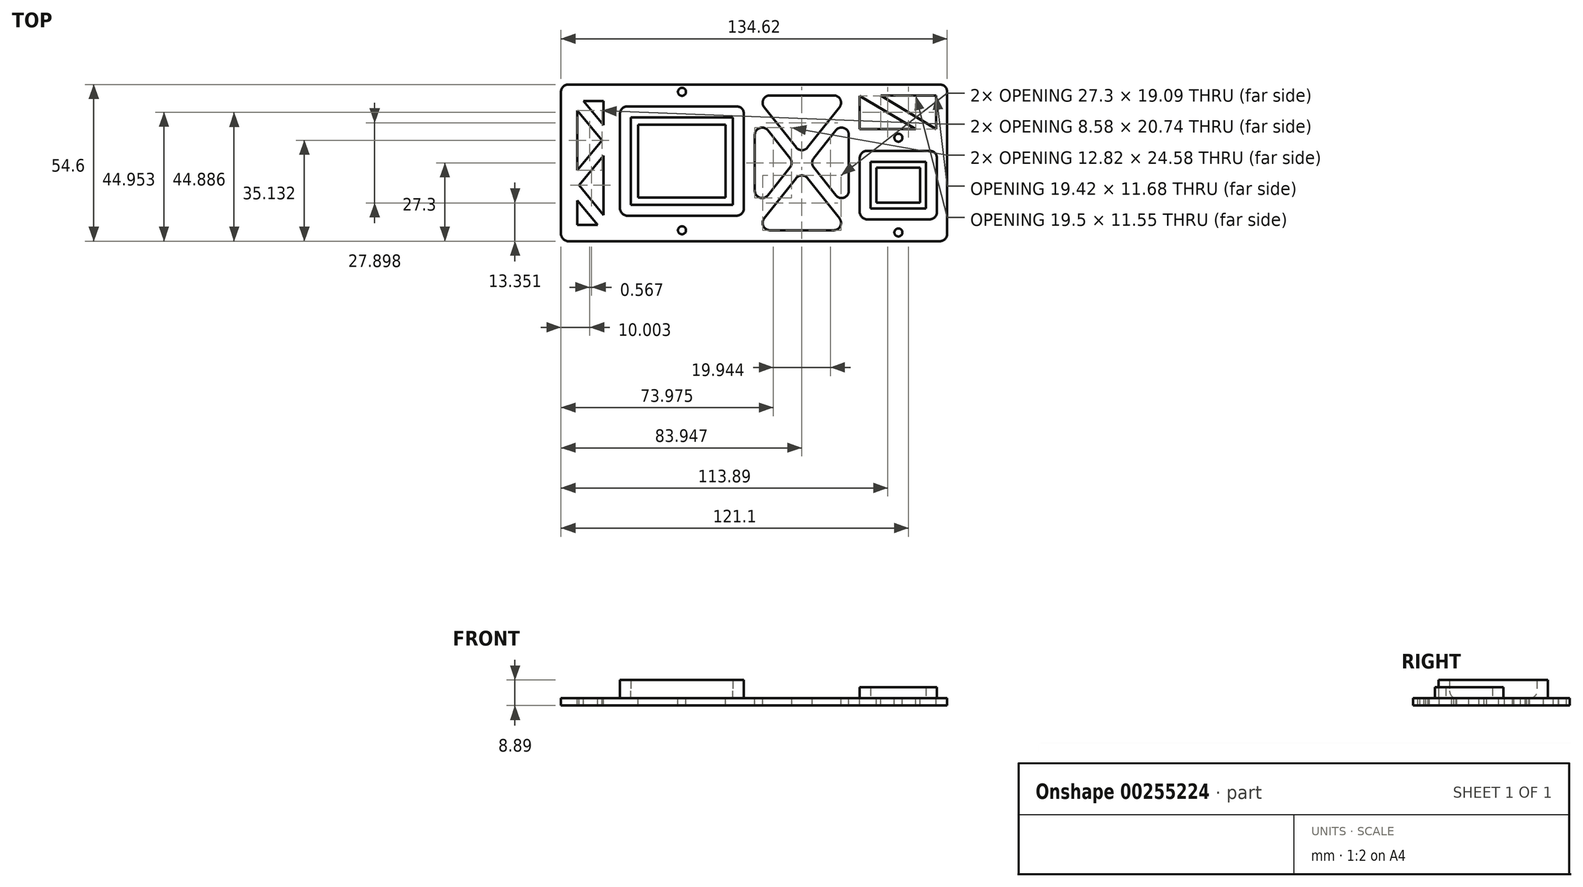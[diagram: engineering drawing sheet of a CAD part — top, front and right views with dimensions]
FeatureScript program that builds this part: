
annotation { "Feature Type Name" : "Feature", "Feature Type Description" : "" }
export const myFeature = defineFeature(function(context is Context, id is Id, definition is map)
    precondition{}
    {
        {
            var Q0;
            Q0=qCreatedBy(makeId("Top.planeOp"),FACE);
            var sketch = newSketch(context, id + "F0", { "sketchPlane" : qUnion([Q0])});
            skLineSegment(sketch, "E0.bottom", {"start": v(67.31, 27.3) * mm, "end": v(-67.31, 27.3) * mm});
            skLineSegment(sketch, "E0.top", {"start": v(67.31, -27.3) * mm, "end": v(-67.31, -27.3) * mm});
            skLineSegment(sketch, "E0.left", {"start": v(67.31, 27.3) * mm, "end": v(67.31, -27.3) * mm});
            skLineSegment(sketch, "E0.right", {"start": v(-67.31, 27.3) * mm, "end": v(-67.31, -27.3) * mm});
            skPoint(sketch, "E0.middle", {"position": v(0, 0) * mm});
            skSolve(sketch);
        }
        {
            var Q0;
            Q0=makeQuery(id+"F0.imprint","IMPRINT",FACE,{"disambiguationData":[TD([[makeQuery(id+"F0.imprint","IMPRINT",EDGE,{"derivedFrom":sQuery(id+"F0.wireOp",EDGE,"E0.bottom")}),1.0]])]});
            extrude(context, id + "F1", {"entities" : qUnion([Q0]), "oppositeDirection" : true, "depth" : 2.54 * mm});
        }
        {
            var Q0;
            Q0=makeQuery(id+"F1.opExtrude","CAP_FACE",FACE,{"disambiguationData":[OSD([sQuery(id+"F0.wireOp",EDGE,"E0.bottom"),sQuery(id+"F0.wireOp",EDGE,"E0.top"),sQuery(id+"F0.wireOp",EDGE,"E0.left"),sQuery(id+"F0.wireOp",EDGE,"E0.right")])],"isStart":true});
            var sketch = newSketch(context, id + "F2", { "sketchPlane" : qUnion([Q0])});
            skLineSegment(sketch, "E1.bottom", {"start": v(-7.37, -14.6) * mm, "end": v(-42.93, -14.6) * mm});
            skLineSegment(sketch, "E1.top", {"start": v(-7.37, 15.88) * mm, "end": v(-42.93, 15.88) * mm});
            skLineSegment(sketch, "E1.left", {"start": v(-7.37, -14.6) * mm, "end": v(-7.37, 15.88) * mm});
            skLineSegment(sketch, "E1.right", {"start": v(-42.93, -14.6) * mm, "end": v(-42.93, 15.88) * mm});
            skPoint(sketch, "E1.middle", {"position": v(-25.15, 0.64) * mm});
            skPoint(sketch, "E2.0", {"position": v(-67.31, -27.3) * mm});
            skLineSegment(sketch, "E3.bottom", {"start": v(59.94, -15.87) * mm, "end": v(40.64, -15.87) * mm});
            skLineSegment(sketch, "E3.top", {"start": v(59.94, 0.38) * mm, "end": v(40.64, 0.38) * mm});
            skLineSegment(sketch, "E3.left", {"start": v(59.94, -15.87) * mm, "end": v(59.94, 0.38) * mm});
            skLineSegment(sketch, "E3.right", {"start": v(40.64, -15.87) * mm, "end": v(40.64, 0.38) * mm});
            skPoint(sketch, "E3.middle", {"position": v(50.3, -7.75) * mm});
            skLineSegment(sketch, "E4.0", {"start": v(-46.74, -18.41) * mm, "end": v(-46.74, 19.69) * mm});
            skLineSegment(sketch, "E4.1", {"start": v(-3.56, -18.41) * mm, "end": v(-46.74, -18.41) * mm});
            skLineSegment(sketch, "E4.2", {"start": v(-3.56, -18.41) * mm, "end": v(-3.56, 19.69) * mm});
            skLineSegment(sketch, "E4.3", {"start": v(-3.56, 19.69) * mm, "end": v(-46.74, 19.69) * mm});
            skLineSegment(sketch, "E5.0", {"start": v(63.75, -19.68) * mm, "end": v(63.75, 4.2) * mm});
            skLineSegment(sketch, "E5.1", {"start": v(63.75, -19.68) * mm, "end": v(36.83, -19.68) * mm});
            skLineSegment(sketch, "E5.2", {"start": v(36.83, -19.68) * mm, "end": v(36.83, 4.2) * mm});
            skLineSegment(sketch, "E5.3", {"start": v(63.75, 4.2) * mm, "end": v(36.83, 4.2) * mm});
            skCircle(sketch, "E6", {"center": v(-25.15, 24.77) * mm, "radius": 1.4 * mm});
            skCircle(sketch, "E7", {"center": v(-25.15, -23.5) * mm, "radius": 1.4 * mm});
            skCircle(sketch, "E8", {"center": v(50.3, 8.76) * mm, "radius": 1.4 * mm});
            skCircle(sketch, "E9", {"center": v(50.3, -24.26) * mm, "radius": 1.4 * mm});
            skPoint(sketch, "E10", {"position": v(-25.15, 19.69) * mm});
            skPoint(sketch, "E11", {"position": v(50.3, -19.68) * mm});
            skLineSegment(sketch, "E12", {"start": v(50.3, 8.76) * mm, "end": v(50.3, -7.75) * mm, "construction": true});
            skLineSegment(sketch, "E13", {"start": v(50.3, -24.26) * mm, "end": v(50.3, -7.75) * mm, "construction": true});
            skLineSegment(sketch, "E14", {"start": v(-25.15, 24.77) * mm, "end": v(-25.15, 0.64) * mm, "construction": true});
            skLineSegment(sketch, "E15", {"start": v(-25.15, -23.5) * mm, "end": v(-25.15, 0.64) * mm, "construction": true});
            skSolve(sketch);
        }
        {
            var Q0;
            Q0=makeQuery(id+"F2.imprint","IMPRINT",FACE,{"disambiguationData":[TD([[makeQuery(id+"F2.imprint","IMPRINT",EDGE,{"derivedFrom":sQuery(id+"F2.wireOp",EDGE,"E6")}),1.0]])]});
            var Q1;
            Q1=makeQuery(id+"F2.imprint","IMPRINT",FACE,{"disambiguationData":[TD([[makeQuery(id+"F2.imprint","IMPRINT",EDGE,{"derivedFrom":sQuery(id+"F2.wireOp",EDGE,"E7")}),1.0]])]});
            var Q2;
            Q2=makeQuery(id+"F2.imprint","IMPRINT",FACE,{"disambiguationData":[TD([[makeQuery(id+"F2.imprint","IMPRINT",EDGE,{"derivedFrom":sQuery(id+"F2.wireOp",EDGE,"E8")}),1.0]])]});
            var Q3;
            Q3=makeQuery(id+"F2.imprint","IMPRINT",FACE,{"disambiguationData":[TD([[makeQuery(id+"F2.imprint","IMPRINT",EDGE,{"derivedFrom":sQuery(id+"F2.wireOp",EDGE,"E9")}),1.0]])]});
            extrude(context, id + "F3", {"entities" : qUnion([Q0, Q1, Q2, Q3]), "operationType" : NewBodyOperationType.REMOVE, "endBound" : BoundingType.THROUGH_ALL, "oppositeDirection" : true, "depth" : 25.4 * mm});
        }
        {
            var Q0;
            Q0=makeQuery(id+"F2.imprint","IMPRINT",FACE,{"disambiguationData":[TD([[makeQuery(id+"F2.imprint","IMPRINT",EDGE,{"derivedFrom":sQuery(id+"F2.wireOp",EDGE,"E1.bottom")}),1.0]])]});
            extrude(context, id + "F4", {"entities" : qUnion([Q0]), "operationType" : NewBodyOperationType.ADD, "depth" : 6.35 * mm});
        }
        {
            var Q0;
            Q0=makeQuery(id+"F2.imprint","IMPRINT",FACE,{"disambiguationData":[TD([[makeQuery(id+"F2.imprint","IMPRINT",EDGE,{"derivedFrom":sQuery(id+"F2.wireOp",EDGE,"E3.bottom")}),1.0]])]});
            extrude(context, id + "F5", {"entities" : qUnion([Q0]), "operationType" : NewBodyOperationType.ADD, "depth" : 3.8 * mm});
        }
        {
            var Q0;
            {var subQ4=sQuery(id+"F0.wireOp",EDGE,"E0.bottom");var subQ5=makeQuery(id+"F1.opExtrude","SWEPT_FACE",FACE,{"disambiguationData":[OSD([subQ4])]});var subQ6=sQuery(id+"F0.wireOp",EDGE,"E0.top");var subQ10=sQuery(id+"F0.wireOp",EDGE,"E0.right");var subQ12=sQuery(id+"F0.wireOp",EDGE,"E0.left");Q0=makeQuery(id+"F5.boolean.opBoolean","SPLIT",FACE,{"disambiguationData":[TD([subQ5])],"derivedFrom":makeQuery(id+"F4.boolean.opBoolean","SPLIT",FACE,{"disambiguationData":[TD([subQ5])],"derivedFrom":makeQuery(id+"F1.opExtrude","CAP_FACE",FACE,{"disambiguationData":[OSD([subQ4,subQ6,subQ12,subQ10])],"isStart":true})})});}
            var sketch = newSketch(context, id + "F6", { "sketchPlane" : qUnion([Q0])});
            skLineSegment(sketch, "E16.0", {"start": v(-3.56, 19.69) * mm, "end": v(-46.74, 19.69) * mm});
            skLineSegment(sketch, "E17.0", {"start": v(-3.56, -18.41) * mm, "end": v(-46.74, -18.41) * mm});
            skLineSegment(sketch, "E18.0", {"start": v(63.75, 4.2) * mm, "end": v(36.83, 4.2) * mm});
            skPoint(sketch, "E19.0", {"position": v(50.3, -19.68) * mm});
            skLineSegment(sketch, "E20.0", {"start": v(63.75, -19.68) * mm, "end": v(36.83, -19.68) * mm});
            skLineSegment(sketch, "E21.0", {"start": v(67.31, -27.3) * mm, "end": v(-67.31, -27.3) * mm});
            skLineSegment(sketch, "E22.0", {"start": v(67.31, 27.3) * mm, "end": v(-67.31, 27.3) * mm});
            skLineSegment(sketch, "E23.bottom", {"start": v(0.25, 23.5) * mm, "end": v(33.02, 23.5) * mm});
            skLineSegment(sketch, "E23.top", {"start": v(0.25, -23.5) * mm, "end": v(33.02, -23.5) * mm});
            skLineSegment(sketch, "E23.left", {"start": v(0.25, 23.5) * mm, "end": v(0.25, -23.5) * mm});
            skLineSegment(sketch, "E23.right", {"start": v(33.02, 23.5) * mm, "end": v(33.02, -23.5) * mm});
            skLineSegment(sketch, "E24.bottom", {"start": v(36.83, 23.5) * mm, "end": v(63.5, 23.5) * mm, "construction": true});
            skLineSegment(sketch, "E24.top", {"start": v(36.83, 11.81) * mm, "end": v(63.5, 11.81) * mm, "construction": true});
            skLineSegment(sketch, "E24.left", {"start": v(36.83, 23.5) * mm, "end": v(36.83, 11.81) * mm, "construction": true});
            skLineSegment(sketch, "E24.right", {"start": v(63.5, 23.5) * mm, "end": v(63.5, 11.81) * mm, "construction": true});
            skPoint(sketch, "E25", {"position": v(16.64, -23.5) * mm});
            skCircle(sketch, "E26", {"center": v(16.64, 0) * mm, "radius": 2.86 * mm, "construction": true});
            skLineSegment(sketch, "E27", {"start": v(0.25, 23.5) * mm, "end": v(16.64, 2.86) * mm});
            skLineSegment(sketch, "E28", {"start": v(16.64, 2.86) * mm, "end": v(33.02, 23.5) * mm});
            skLineSegment(sketch, "E29", {"start": v(0.25, -23.5) * mm, "end": v(16.64, -2.86) * mm});
            skLineSegment(sketch, "E30", {"start": v(16.64, -2.86) * mm, "end": v(33.02, -23.5) * mm});
            skLineSegment(sketch, "E31", {"start": v(0.25, 17.04) * mm, "end": v(13.78, 0) * mm});
            skLineSegment(sketch, "E32", {"start": v(13.78, 0) * mm, "end": v(0.25, -17.04) * mm});
            skLineSegment(sketch, "E33", {"start": v(33.02, 17.04) * mm, "end": v(19.5, 0) * mm});
            skLineSegment(sketch, "E34", {"start": v(19.5, 0) * mm, "end": v(33.02, -17.04) * mm});
            skLineSegment(sketch, "E35", {"start": v(44.08, 23.5) * mm, "end": v(63.5, 11.81) * mm});
            skLineSegment(sketch, "E36", {"start": v(36.83, 23.36) * mm, "end": v(56.33, 11.81) * mm});
            skPoint(sketch, "E37", {"position": v(50.17, 17.65) * mm});
            skPoint(sketch, "E37.positionSnap0", {"position": v(36.83, 17.65) * mm});
            skPoint(sketch, "E38", {"position": v(50.17, 11.81) * mm});
            skLineSegment(sketch, "E39", {"start": v(50.17, 17.65) * mm, "end": v(51.34, 19.13) * mm, "construction": true});
            skLineSegment(sketch, "E40", {"start": v(50.16, 17.65) * mm, "end": v(49.2, 16.03) * mm, "construction": true});
            skLineSegment(sketch, "E41", {"start": v(44.08, 23.5) * mm, "end": v(42.12, 20.23) * mm, "construction": true});
            skLineSegment(sketch, "E42", {"start": v(36.83, 23.36) * mm, "end": v(36.83, 11.81) * mm});
            skLineSegment(sketch, "E43", {"start": v(36.83, 11.81) * mm, "end": v(56.33, 11.81) * mm});
            skLineSegment(sketch, "E44", {"start": v(63.5, 11.81) * mm, "end": v(63.5, 23.5) * mm});
            skLineSegment(sketch, "E45", {"start": v(63.5, 23.5) * mm, "end": v(44.08, 23.5) * mm});
            skPoint(sketch, "E46", {"position": v(-25.15, 0.64) * mm});
            skPoint(sketch, "E46.positionSnap0", {"position": v(-25.15, 19.69) * mm});
            skPoint(sketch, "E47", {"position": v(50.3, -7.75) * mm});
            skPoint(sketch, "E47.positionSnap0", {"position": v(50.3, 4.2) * mm});
            skPoint(sketch, "E48", {"position": v(36.83, -7.75) * mm});
            skPoint(sketch, "E49", {"position": v(-46.74, 0.64) * mm});
            skLineSegment(sketch, "E50.bottom", {"start": v(-9.9, 13.34) * mm, "end": v(-40.39, 13.34) * mm});
            skLineSegment(sketch, "E50.top", {"start": v(-9.9, -12.07) * mm, "end": v(-40.39, -12.07) * mm});
            skLineSegment(sketch, "E50.left", {"start": v(-9.9, 13.34) * mm, "end": v(-9.9, -12.07) * mm});
            skLineSegment(sketch, "E50.right", {"start": v(-40.39, 13.34) * mm, "end": v(-40.39, -12.07) * mm});
            skLineSegment(sketch, "E51.bottom", {"start": v(57.91, -1.65) * mm, "end": v(42.67, -1.65) * mm});
            skLineSegment(sketch, "E51.top", {"start": v(57.91, -13.84) * mm, "end": v(42.67, -13.84) * mm});
            skLineSegment(sketch, "E51.left", {"start": v(57.91, -1.65) * mm, "end": v(57.91, -13.84) * mm});
            skLineSegment(sketch, "E51.right", {"start": v(42.67, -1.65) * mm, "end": v(42.67, -13.84) * mm});
            skLineSegment(sketch, "E52.bottom", {"start": v(-63.5, 23.5) * mm, "end": v(-50.55, 23.5) * mm});
            skLineSegment(sketch, "E52.top", {"start": v(-63.5, -23.5) * mm, "end": v(-50.55, -23.5) * mm});
            skLineSegment(sketch, "E53", {"start": v(-63.5, 23.5) * mm, "end": v(-50.55, 7.83) * mm});
            skLineSegment(sketch, "E54", {"start": v(-50.55, 7.83) * mm, "end": v(-63.5, -7.83) * mm});
            skLineSegment(sketch, "E55", {"start": v(-63.5, -7.83) * mm, "end": v(-50.55, -23.5) * mm});
            skLineSegment(sketch, "E56", {"start": v(-63.5, 23.5) * mm, "end": v(-63.5, -7.83) * mm});
            skLineSegment(sketch, "E57", {"start": v(-63.5, -7.83) * mm, "end": v(-63.5, -23.5) * mm});
            skLineSegment(sketch, "E58", {"start": v(-50.55, -23.5) * mm, "end": v(-50.55, 7.83) * mm});
            skLineSegment(sketch, "E59", {"start": v(-50.55, 7.83) * mm, "end": v(-50.55, 23.5) * mm});
            skLineSegment(sketch, "E60.0", {"start": v(-52.45, 2.54) * mm, "end": v(-61.03, -7.83) * mm});
            skLineSegment(sketch, "E60.1", {"start": v(-52.45, -18.2) * mm, "end": v(-52.45, 2.54) * mm});
            skLineSegment(sketch, "E60.2", {"start": v(-61.03, -7.83) * mm, "end": v(-52.45, -18.2) * mm});
            skLineSegment(sketch, "E61.0", {"start": v(-59.45, 21.59) * mm, "end": v(-52.45, 13.12) * mm});
            skLineSegment(sketch, "E61.1", {"start": v(-59.45, 21.59) * mm, "end": v(-52.45, 21.59) * mm});
            skLineSegment(sketch, "E61.2", {"start": v(-52.45, 13.12) * mm, "end": v(-52.45, 21.59) * mm});
            skLineSegment(sketch, "E62.0", {"start": v(-61.6, 18.2) * mm, "end": v(-53.02, 7.83) * mm});
            skLineSegment(sketch, "E62.1", {"start": v(-61.6, 18.2) * mm, "end": v(-61.6, -2.54) * mm});
            skLineSegment(sketch, "E62.2", {"start": v(-53.02, 7.83) * mm, "end": v(-61.6, -2.54) * mm});
            skLineSegment(sketch, "E63.0", {"start": v(-61.6, -13.12) * mm, "end": v(-54.6, -21.59) * mm});
            skLineSegment(sketch, "E63.1", {"start": v(-61.6, -13.12) * mm, "end": v(-61.6, -21.59) * mm});
            skLineSegment(sketch, "E63.2", {"start": v(-61.6, -21.59) * mm, "end": v(-54.6, -21.59) * mm});
            skSolve(sketch);
        }
        {
            var Q0;
            Q0=makeQuery(id+"F6.imprint","IMPRINT",FACE,{"disambiguationData":[TD([[makeQuery(id+"F6.imprint","IMPRINT",EDGE,{"derivedFrom":sQuery(id+"F6.wireOp",EDGE,"qbaPRZ6K-c828-ytG8-pBS6-OXfPjTGeBxSN.bottom")}),-1.0]])]});
            var Q1;
            Q1=makeQuery(id+"F6.imprint","IMPRINT",FACE,{"disambiguationData":[TD([[makeQuery(id+"F6.imprint","IMPRINT",EDGE,{"derivedFrom":sQuery(id+"F6.wireOp",EDGE,"puD6v0uv-njwl-qLN5-xzXm-XjD75bYEGFfy")}),-1.0]])]});
            var Q2;
            Q2=makeQuery(id+"F6.imprint","IMPRINT",FACE,{"disambiguationData":[TD([[makeQuery(id+"F6.imprint","IMPRINT",EDGE,{"derivedFrom":sQuery(id+"F6.wireOp",EDGE,"U4YJNHmE-5GH2-H4sl-fmaE-EzOXsRJQINV2")}),1.0]])]});
            var Q3;
            Q3=makeQuery(id+"F6.imprint","IMPRINT",FACE,{"disambiguationData":[TD([[makeQuery(id+"F6.imprint","IMPRINT",EDGE,{"derivedFrom":sQuery(id+"F6.wireOp",EDGE,"qbaPRZ6K-c828-ytG8-pBS6-OXfPjTGeBxSN.top")}),1.0]])]});
            var Q4;
            {var subQ0=sQuery(id+"F6.wireOp",EDGE,"E31");Q4=makeQuery(id+"F6.imprint","IMPRINT",FACE,{"disambiguationData":[TD([[makeQuery(id+"F6.imprint","IMPRINT",EDGE,{"derivedFrom":subQ0}),-1.0]])]});}
            var Q5;
            Q5=makeQuery(id+"F6.imprint","IMPRINT",FACE,{"disambiguationData":[TD([[makeQuery(id+"F6.imprint","IMPRINT",EDGE,{"derivedFrom":sQuery(id+"F6.wireOp",EDGE,"E23.bottom")}),-1.0]])]});
            var Q6;
            {var subQ0=sQuery(id+"F6.wireOp",EDGE,"E33");Q6=makeQuery(id+"F6.imprint","IMPRINT",FACE,{"disambiguationData":[TD([[makeQuery(id+"F6.imprint","IMPRINT",EDGE,{"derivedFrom":subQ0}),1.0]])]});}
            var Q7;
            Q7=makeQuery(id+"F6.imprint","IMPRINT",FACE,{"disambiguationData":[TD([[makeQuery(id+"F6.imprint","IMPRINT",EDGE,{"derivedFrom":sQuery(id+"F6.wireOp",EDGE,"E23.top")}),1.0]])]});
            var Q8;
            Q8=makeQuery(id+"F6.imprint","IMPRINT",FACE,{"disambiguationData":[TD([[makeQuery(id+"F6.imprint","IMPRINT",EDGE,{"derivedFrom":sQuery(id+"F6.wireOp",EDGE,"E36")}),-1.0]])]});
            var Q9;
            Q9=makeQuery(id+"F6.imprint","IMPRINT",FACE,{"disambiguationData":[TD([[makeQuery(id+"F6.imprint","IMPRINT",EDGE,{"derivedFrom":sQuery(id+"F6.wireOp",EDGE,"E35")}),1.0]])]});
            var Q10;
            Q10=makeQuery(id+"F6.imprint","IMPRINT",FACE,{"disambiguationData":[TD([[makeQuery(id+"F6.imprint","IMPRINT",EDGE,{"derivedFrom":sQuery(id+"F6.wireOp",EDGE,"E50.bottom")}),1.0]])]});
            var Q11;
            Q11=makeQuery(id+"F6.imprint","IMPRINT",FACE,{"disambiguationData":[TD([[makeQuery(id+"F6.imprint","IMPRINT",EDGE,{"derivedFrom":sQuery(id+"F6.wireOp",EDGE,"E51.bottom")}),1.0]])]});
            var Q12;
            Q12=makeQuery(id+"F6.imprint","IMPRINT",FACE,{"disambiguationData":[TD([[makeQuery(id+"F6.imprint","IMPRINT",EDGE,{"derivedFrom":sQuery(id+"F6.wireOp",EDGE,"E62.0")}),-1.0]])]});
            var Q13;
            Q13=makeQuery(id+"F6.imprint","IMPRINT",FACE,{"disambiguationData":[TD([[makeQuery(id+"F6.imprint","IMPRINT",EDGE,{"derivedFrom":sQuery(id+"F6.wireOp",EDGE,"E61.0")}),1.0]])]});
            var Q14;
            Q14=makeQuery(id+"F6.imprint","IMPRINT",FACE,{"disambiguationData":[TD([[makeQuery(id+"F6.imprint","IMPRINT",EDGE,{"derivedFrom":sQuery(id+"F6.wireOp",EDGE,"E60.0")}),1.0]])]});
            var Q15;
            Q15=makeQuery(id+"F6.imprint","IMPRINT",FACE,{"disambiguationData":[TD([[makeQuery(id+"F6.imprint","IMPRINT",EDGE,{"derivedFrom":sQuery(id+"F6.wireOp",EDGE,"E63.0")}),-1.0]])]});
            extrude(context, id + "F7", {"entities" : qUnion([Q0, Q1, Q2, Q3, Q4, Q5, Q6, Q7, Q8, Q9, Q10, Q11, Q12, Q13, Q14, Q15]), "operationType" : NewBodyOperationType.REMOVE, "endBound" : BoundingType.THROUGH_ALL, "oppositeDirection" : true, "depth" : 25.4 * mm});
        }
        {
            var Q0;
            Q0=makeQuery(id+"F4.opExtrude","CAP_EDGE",EDGE,{"disambiguationData":[OSD([sQuery(id+"F2.wireOp",EDGE,"E4.1")])],"isStart":true});
            var Q1;
            Q1=makeQuery(id+"F4.opExtrude","CAP_EDGE",EDGE,{"disambiguationData":[OSD([sQuery(id+"F2.wireOp",EDGE,"E4.0")])],"isStart":true});
            var Q2;
            Q2=makeQuery(id+"F5.opExtrude","CAP_EDGE",EDGE,{"disambiguationData":[OSD([sQuery(id+"F2.wireOp",EDGE,"E5.1")])],"isStart":true});
            var Q3;
            Q3=makeQuery(id+"F5.opExtrude","CAP_EDGE",EDGE,{"disambiguationData":[OSD([sQuery(id+"F2.wireOp",EDGE,"E5.2")])],"isStart":true});
            var Q4;
            Q4=makeQuery(id+"F4.opExtrude","CAP_EDGE",EDGE,{"disambiguationData":[OSD([sQuery(id+"F2.wireOp",EDGE,"E4.3")])],"isStart":true});
            var Q5;
            Q5=makeQuery(id+"F4.opExtrude","CAP_EDGE",EDGE,{"disambiguationData":[OSD([sQuery(id+"F2.wireOp",EDGE,"E4.2")])],"isStart":true});
            var Q6;
            Q6=makeQuery(id+"F5.opExtrude","CAP_EDGE",EDGE,{"disambiguationData":[OSD([sQuery(id+"F2.wireOp",EDGE,"E5.0")])],"isStart":true});
            var Q7;
            Q7=makeQuery(id+"F5.opExtrude","CAP_EDGE",EDGE,{"disambiguationData":[OSD([sQuery(id+"F2.wireOp",EDGE,"E5.3")])],"isStart":true});
            var Q8;
            Q8=makeQuery(id+"F5.opExtrude","SWEPT_EDGE",EDGE,{"disambiguationData":[OSD([sQuery(id+"F2.wireOp",EDGE,"E5.0"),sQuery(id+"F2.wireOp",EDGE,"E5.3")])]});
            var Q9;
            Q9=makeQuery(id+"F5.opExtrude","SWEPT_EDGE",EDGE,{"disambiguationData":[OSD([sQuery(id+"F2.wireOp",EDGE,"E5.0"),sQuery(id+"F2.wireOp",EDGE,"E5.1")])]});
            var Q10;
            Q10=makeQuery(id+"F4.opExtrude","SWEPT_EDGE",EDGE,{"disambiguationData":[OSD([sQuery(id+"F2.wireOp",EDGE,"E4.2"),sQuery(id+"F2.wireOp",EDGE,"E4.3")])]});
            var Q11;
            Q11=makeQuery(id+"F4.opExtrude","SWEPT_EDGE",EDGE,{"disambiguationData":[OSD([sQuery(id+"F2.wireOp",EDGE,"E4.1"),sQuery(id+"F2.wireOp",EDGE,"E4.2")])]});
            var Q12;
            Q12=makeQuery(id+"F5.opExtrude","SWEPT_EDGE",EDGE,{"disambiguationData":[OSD([sQuery(id+"F2.wireOp",EDGE,"E5.1"),sQuery(id+"F2.wireOp",EDGE,"E5.2")])]});
            var Q13;
            Q13=makeQuery(id+"F4.opExtrude","SWEPT_EDGE",EDGE,{"disambiguationData":[OSD([sQuery(id+"F2.wireOp",EDGE,"E4.0"),sQuery(id+"F2.wireOp",EDGE,"E4.1")])]});
            var Q14;
            Q14=makeQuery(id+"F4.opExtrude","SWEPT_EDGE",EDGE,{"disambiguationData":[OSD([sQuery(id+"F2.wireOp",EDGE,"E4.0"),sQuery(id+"F2.wireOp",EDGE,"E4.3")])]});
            var Q15;
            Q15=makeQuery(id+"F5.opExtrude","SWEPT_EDGE",EDGE,{"disambiguationData":[OSD([sQuery(id+"F2.wireOp",EDGE,"E5.2"),sQuery(id+"F2.wireOp",EDGE,"E5.3")])]});
            var Q16;
            Q16=makeQuery(id+"F4.opExtrude","CAP_EDGE",EDGE,{"disambiguationData":[OSD([sQuery(id+"F2.wireOp",EDGE,"E1.top")])],"isStart":true});
            var Q17;
            Q17=makeQuery(id+"F4.opExtrude","CAP_EDGE",EDGE,{"disambiguationData":[OSD([sQuery(id+"F2.wireOp",EDGE,"E1.bottom")])],"isStart":true});
            var Q18;
            Q18=makeQuery(id+"F1.opExtrude","SWEPT_EDGE",EDGE,{"disambiguationData":[OSD([sQuery(id+"F0.wireOp",EDGE,"E0.top"),sQuery(id+"F0.wireOp",EDGE,"E0.right")])]});
            var Q19;
            Q19=makeQuery(id+"F1.opExtrude","SWEPT_EDGE",EDGE,{"disambiguationData":[OSD([sQuery(id+"F0.wireOp",EDGE,"E0.bottom"),sQuery(id+"F0.wireOp",EDGE,"E0.right")])]});
            var Q20;
            Q20=makeQuery(id+"F1.opExtrude","SWEPT_EDGE",EDGE,{"disambiguationData":[OSD([sQuery(id+"F0.wireOp",EDGE,"E0.bottom"),sQuery(id+"F0.wireOp",EDGE,"E0.left")])]});
            var Q21;
            Q21=makeQuery(id+"F1.opExtrude","SWEPT_EDGE",EDGE,{"disambiguationData":[OSD([sQuery(id+"F0.wireOp",EDGE,"E0.top"),sQuery(id+"F0.wireOp",EDGE,"E0.left")])]});
            fillet(context, id + "F8", {"entities" : qUnion([Q0, Q1, Q2, Q3, Q4, Q5, Q6, Q7, Q8, Q9, Q10, Q11, Q12, Q13, Q14, Q15, Q16, Q17, Q18, Q19, Q20, Q21]), "radius" : 2.54 * mm, "tangentPropagation" : true, "allowEdgeOverflow" : false});
        }
        {
            var Q0;
            Q0=makeQuery(id+"F7.boolean.opBoolean","COPY",EDGE,{"derivedFrom":makeQuery(id+"F7.opExtrude","SWEPT_EDGE",EDGE,{"disambiguationData":[OSD([sQuery(id+"F6.wireOp",EDGE,"E23.bottom"),sQuery(id+"F6.wireOp",EDGE,"E23.right"),sQuery(id+"F6.wireOp",EDGE,"E28")])]})});
            var Q1;
            Q1=makeQuery(id+"F7.boolean.opBoolean","COPY",EDGE,{"derivedFrom":makeQuery(id+"F7.opExtrude","SWEPT_EDGE",EDGE,{"disambiguationData":[OSD([sQuery(id+"F6.wireOp",EDGE,"E31"),sQuery(id+"F6.wireOp",EDGE,"E32")])]})});
            var Q2;
            Q2=makeQuery(id+"F7.boolean.opBoolean","COPY",EDGE,{"derivedFrom":makeQuery(id+"F7.opExtrude","SWEPT_EDGE",EDGE,{"disambiguationData":[OSD([sQuery(id+"F6.wireOp",EDGE,"E29"),sQuery(id+"F6.wireOp",EDGE,"E30")])]})});
            var Q3;
            Q3=makeQuery(id+"F7.boolean.opBoolean","COPY",EDGE,{"derivedFrom":makeQuery(id+"F7.opExtrude","SWEPT_EDGE",EDGE,{"disambiguationData":[OSD([sQuery(id+"F6.wireOp",EDGE,"E23.left"),sQuery(id+"F6.wireOp",EDGE,"E31")])]})});
            var Q4;
            Q4=makeQuery(id+"F7.boolean.opBoolean","COPY",EDGE,{"derivedFrom":makeQuery(id+"F7.opExtrude","SWEPT_EDGE",EDGE,{"disambiguationData":[OSD([sQuery(id+"F6.wireOp",EDGE,"E23.right"),sQuery(id+"F6.wireOp",EDGE,"E33")])]})});
            var Q5;
            Q5=makeQuery(id+"F7.boolean.opBoolean","COPY",EDGE,{"derivedFrom":makeQuery(id+"F7.opExtrude","SWEPT_EDGE",EDGE,{"disambiguationData":[OSD([sQuery(id+"F6.wireOp",EDGE,"E23.right"),sQuery(id+"F6.wireOp",EDGE,"E34")])]})});
            var Q6;
            Q6=makeQuery(id+"F7.boolean.opBoolean","COPY",EDGE,{"derivedFrom":makeQuery(id+"F7.opExtrude","SWEPT_EDGE",EDGE,{"disambiguationData":[OSD([sQuery(id+"F6.wireOp",EDGE,"E23.top"),sQuery(id+"F6.wireOp",EDGE,"E23.right"),sQuery(id+"F6.wireOp",EDGE,"E30")])]})});
            var Q7;
            Q7=makeQuery(id+"F7.boolean.opBoolean","COPY",EDGE,{"derivedFrom":makeQuery(id+"F7.opExtrude","SWEPT_EDGE",EDGE,{"disambiguationData":[OSD([sQuery(id+"F6.wireOp",EDGE,"E23.bottom"),sQuery(id+"F6.wireOp",EDGE,"E23.left"),sQuery(id+"F6.wireOp",EDGE,"E27")])]})});
            var Q8;
            Q8=makeQuery(id+"F7.boolean.opBoolean","COPY",EDGE,{"derivedFrom":makeQuery(id+"F7.opExtrude","SWEPT_EDGE",EDGE,{"disambiguationData":[OSD([sQuery(id+"F6.wireOp",EDGE,"E23.top"),sQuery(id+"F6.wireOp",EDGE,"E23.left"),sQuery(id+"F6.wireOp",EDGE,"E29")])]})});
            var Q9;
            Q9=makeQuery(id+"F7.boolean.opBoolean","COPY",EDGE,{"derivedFrom":makeQuery(id+"F7.opExtrude","SWEPT_EDGE",EDGE,{"disambiguationData":[OSD([sQuery(id+"F6.wireOp",EDGE,"E23.left"),sQuery(id+"F6.wireOp",EDGE,"E32")])]})});
            var Q10;
            Q10=makeQuery(id+"F7.boolean.opBoolean","COPY",EDGE,{"derivedFrom":makeQuery(id+"F7.opExtrude","SWEPT_EDGE",EDGE,{"disambiguationData":[OSD([sQuery(id+"F6.wireOp",EDGE,"E33"),sQuery(id+"F6.wireOp",EDGE,"E34")])]})});
            var Q11;
            Q11=makeQuery(id+"F7.boolean.opBoolean","COPY",EDGE,{"derivedFrom":makeQuery(id+"F7.opExtrude","SWEPT_EDGE",EDGE,{"disambiguationData":[OSD([sQuery(id+"F6.wireOp",EDGE,"E27"),sQuery(id+"F6.wireOp",EDGE,"E28")])]})});
            fillet(context, id + "F9", {"entities" : qUnion([Q0, Q1, Q2, Q3, Q4, Q5, Q6, Q7, Q8, Q9, Q10, Q11]), "radius" : 2.54 * mm, "tangentPropagation" : true, "allowEdgeOverflow" : false});
        }
    });
